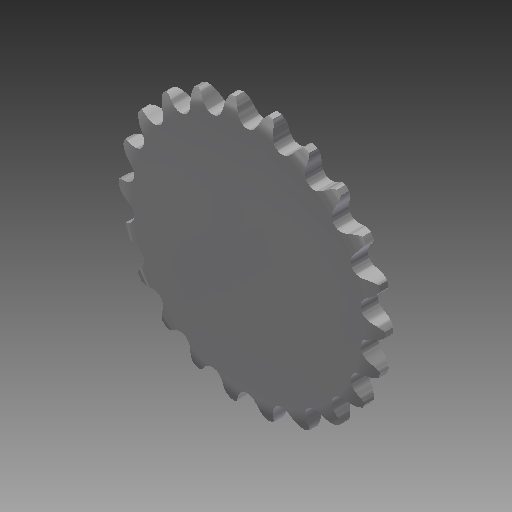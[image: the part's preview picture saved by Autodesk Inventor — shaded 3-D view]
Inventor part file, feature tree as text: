
AUTODESK INVENTOR PART (.ipt)
format: ipt  version: 2017 (Build 210142000, 142)  size: 618,496 bytes
history: native  units: mm
features: other x6, extrude x2, pattern_linear x1, pattern_circular x1
ambient origin geometry x8: Origin, YZ Plane, XZ Plane, XY Plane, X Axis, Y Axis, Z Axis, Center Point
bodies: Solid1 (feature_tree)
feature tree (10):
  other  "Theoretical Tooth Profile"
  other  "Tooth Profile"
  other  "Section Profile"
  other  "Shroud"
  other  "Strand"
  pattern_linear  "Strand Pattern"  Spacing1=44.619381mm  [1 undecoded]
  extrude  "Theoretical Tooth"  Depth=2.855993mm
  extrude  "Tooth"  Depth=1.697355mm
  pattern_circular  "Tooth Pattern"  [2 undecoded]
  other  "Timing Plane"
note: 3 required parameter values undecoded (feature->parameter linkage not recoverable at this tier; creation-order binding heuristic only, values carry confidence <= 0.55)
